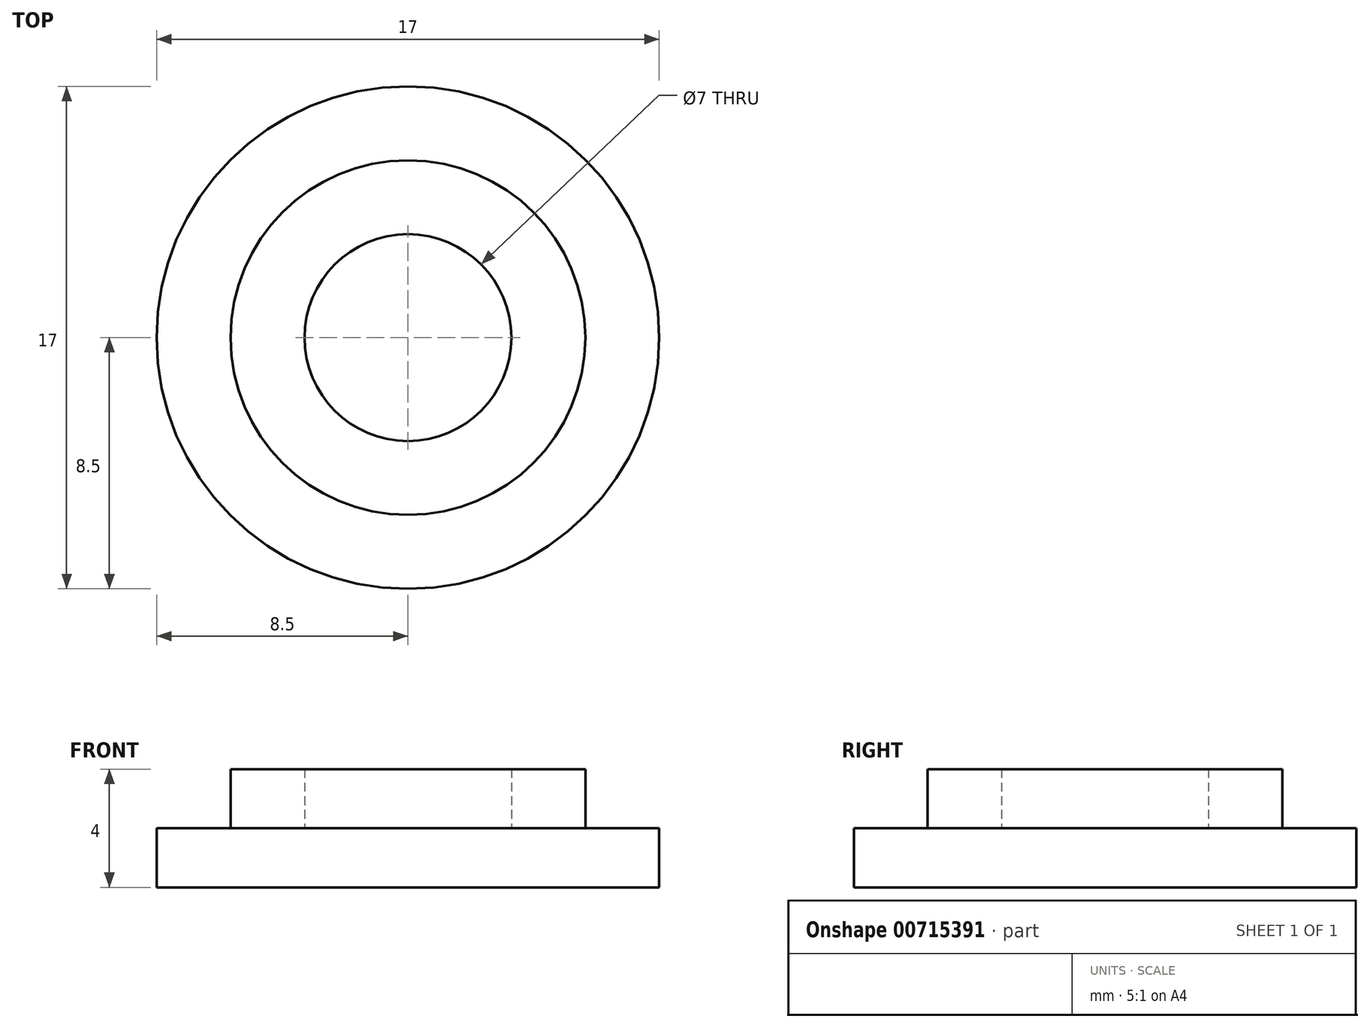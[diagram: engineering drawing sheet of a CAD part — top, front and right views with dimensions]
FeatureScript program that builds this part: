
annotation { "Feature Type Name" : "Feature", "Feature Type Description" : "" }
export const myFeature = defineFeature(function(context is Context, id is Id, definition is map)
    precondition{}
    {
        {
            var Q0;
            Q0=qCreatedBy(makeId("Top.planeOp"),FACE);
            var sketch = newSketch(context, id + "F0", { "sketchPlane" : qUnion([Q0])});
            skCircle(sketch, "E0", {"center": v(0, 0) * mm, "radius": 8.5 * mm});
            skSolve(sketch);
        }
        {
            var Q0;
            Q0=qCreatedBy(makeId("Top.planeOp"),FACE);
            var sketch = newSketch(context, id + "F1", { "sketchPlane" : qUnion([Q0])});
            skCircle(sketch, "E1", {"center": v(0, 0) * mm, "radius": 6 * mm});
            skSolve(sketch);
        }
        {
            var Q0;
            Q0=qCreatedBy(makeId("Top.planeOp"),FACE);
            var sketch = newSketch(context, id + "F2", { "sketchPlane" : qUnion([Q0])});
            skCircle(sketch, "E2", {"center": v(0, 0) * mm, "radius": 3.5 * mm});
            skSolve(sketch);
        }
        {
            var Q0;
            Q0 = qSketchRegion(id + "F0", true);
            var Q1;
            Q1=sQuery(id+"F0.wireOp",EDGE,"E0");
            extrude(context, id + "F3", {"entities" : qUnion([Q0]), "surfaceEntities" : qUnion([Q1]), "oppositeDirection" : true, "depth" : 2 * mm, "offsetDistance" : 25 * mm});
        }
        {
            var Q0;
            Q0 = qSketchRegion(id + "F1", true);
            extrude(context, id + "F4", {"entities" : qUnion([Q0]), "depth" : 2 * mm, "offsetDistance" : 25 * mm});
        }
        {
            var Q0;
            Q0 = qSketchRegion(id + "F2", true);
            extrude(context, id + "F5", {"entities" : qUnion([Q0]), "operationType" : NewBodyOperationType.REMOVE, "depth" : 25 * mm, "offsetDistance" : 25 * mm});
        }
    });
